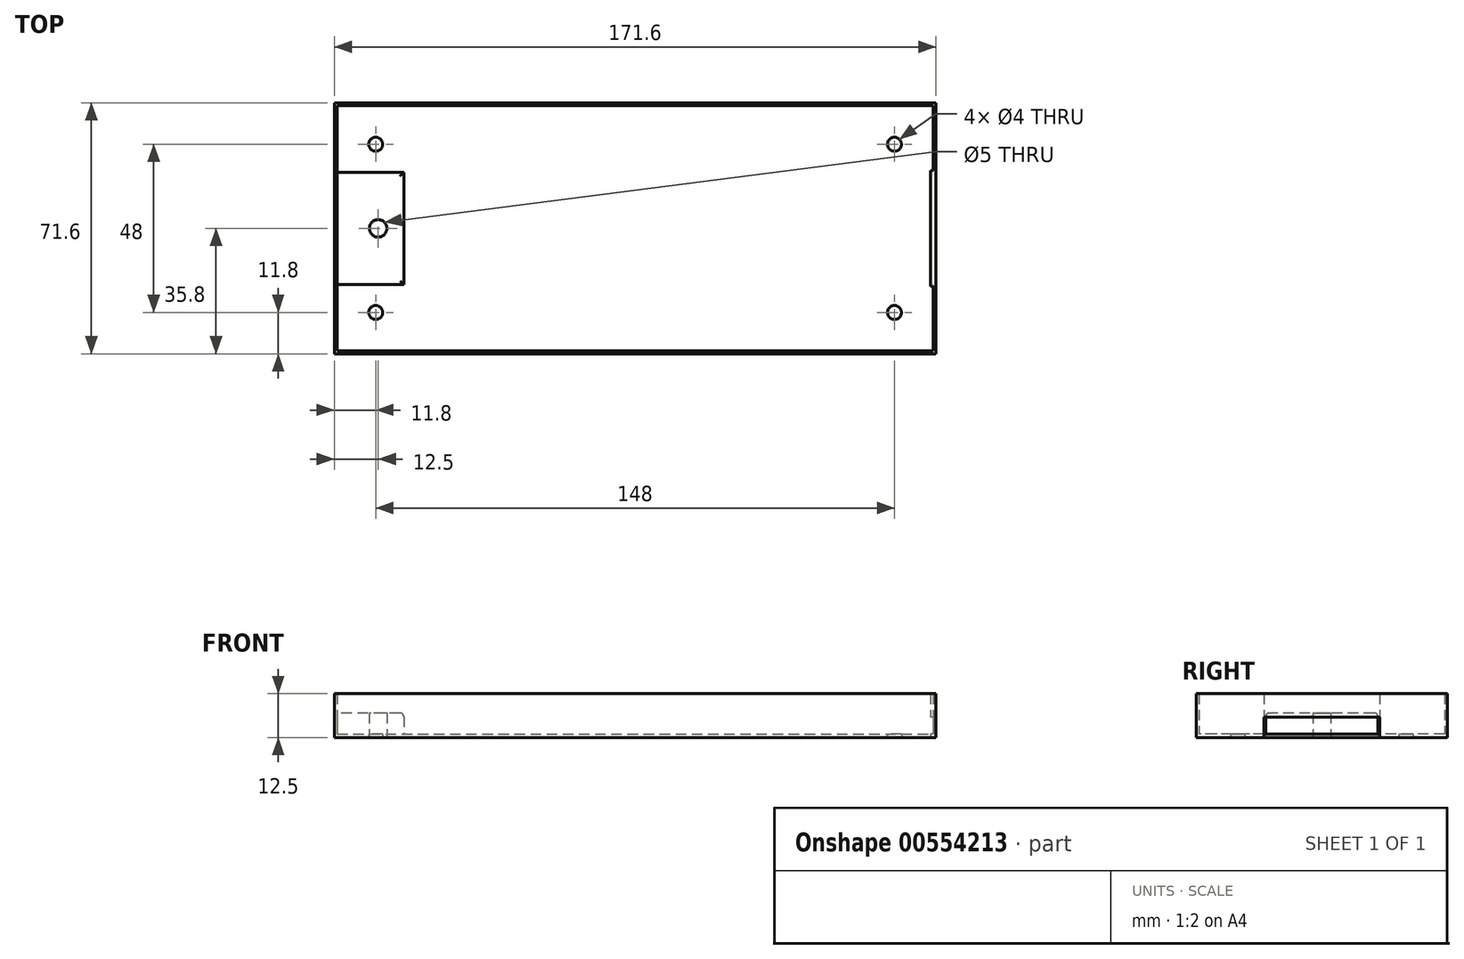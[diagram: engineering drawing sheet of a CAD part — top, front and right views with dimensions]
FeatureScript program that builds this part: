
annotation { "Feature Type Name" : "Feature", "Feature Type Description" : "" }
export const myFeature = defineFeature(function(context is Context, id is Id, definition is map)
    precondition{}
    {
        {
            var Q0;
            Q0=qCreatedBy(makeId("Top.planeOp"),FACE);
            var sketch = newSketch(context, id + "F0", { "sketchPlane" : qUnion([Q0])});
            skLineSegment(sketch, "E0.bottom", {"start": v(-85, 35) * mm, "end": v(85, 35) * mm});
            skLineSegment(sketch, "E0.top", {"start": v(-85, -35) * mm, "end": v(85, -35) * mm});
            skLineSegment(sketch, "E0.left", {"start": v(-85, 35) * mm, "end": v(-85, -35) * mm});
            skLineSegment(sketch, "E0.right", {"start": v(85, 35) * mm, "end": v(85, -35) * mm});
            skPoint(sketch, "E0.middle", {"position": v(0, 0) * mm});
            skCircle(sketch, "E1", {"center": v(74, -24) * mm, "radius": 2 * mm});
            skLineSegment(sketch, "E2", {"start": v(-150.17, 0) * mm, "end": v(130.9, 0) * mm, "construction": true});
            skCircle(sketch, "E3.MirrorC", {"center": v(74, 24) * mm, "radius": 2 * mm});
            skCircle(sketch, "E4", {"center": v(-74, -24) * mm, "radius": 2 * mm});
            skCircle(sketch, "E5.MirrorC", {"center": v(-74, 24) * mm, "radius": 2 * mm});
            skLineSegment(sketch, "E6.0", {"start": v(-85.8, 35.8) * mm, "end": v(85.8, 35.8) * mm});
            skLineSegment(sketch, "E6.1", {"start": v(-85.8, 35.8) * mm, "end": v(-85.8, -35.8) * mm});
            skLineSegment(sketch, "E6.2", {"start": v(-85.8, -35.8) * mm, "end": v(85.8, -35.8) * mm});
            skLineSegment(sketch, "E6.3", {"start": v(85.8, 35.8) * mm, "end": v(85.8, -35.8) * mm});
            skLineSegment(sketch, "E7.bottom", {"start": v(85.8, 16.5) * mm, "end": v(84.3, 16.5) * mm});
            skLineSegment(sketch, "E7.top", {"start": v(85.8, -16.5) * mm, "end": v(84.3, -16.5) * mm});
            skLineSegment(sketch, "E7.left", {"start": v(85.8, 16.5) * mm, "end": v(85.8, -16.5) * mm});
            skLineSegment(sketch, "E7.right", {"start": v(84.3, 16.5) * mm, "end": v(84.3, -16.5) * mm});
            skPoint(sketch, "E7.middle", {"position": v(85.05, 0) * mm});
            skLineSegment(sketch, "E8.bottom", {"start": v(-66, 16) * mm, "end": v(-85, 16) * mm});
            skLineSegment(sketch, "E8.top", {"start": v(-66, -16) * mm, "end": v(-85, -16) * mm});
            skLineSegment(sketch, "E8.left", {"start": v(-66, 16) * mm, "end": v(-66, -16) * mm});
            skLineSegment(sketch, "E8.right", {"start": v(-85, 16) * mm, "end": v(-85, -16) * mm});
            skPoint(sketch, "E8.middle", {"position": v(-85, 0) * mm});
            skCircle(sketch, "E9", {"center": v(-73.3, 0) * mm, "radius": 2.5 * mm});
            skPoint(sketch, "E9.centerSnap0", {"position": v(-75.5, 16) * mm});
            skSolve(sketch);
        }
        {
            var Q0;
            {var subQ3=sQuery(id+"F0.wireOp",EDGE,"E0.bottom");Q0=makeQuery(id+"F0.imprint","IMPRINT",FACE,{"disambiguationData":[TD([[makeQuery(id+"F0.imprint","IMPRINT",EDGE,{"derivedFrom":subQ3}),-1.0]])]});}
            var Q1;
            Q1=makeQuery(id+"F0.imprint","IMPRINT",FACE,{"disambiguationData":[TD([[makeQuery(id+"F0.imprint","IMPRINT",EDGE,{"derivedFrom":sQuery(id+"F0.wireOp",EDGE,"E8.bottom")}),1.0]])]});
            extrude(context, id + "F1", {"entities" : qUnion([Q0, Q1]), "depth" : 1 * mm, "offsetDistance" : 25 * mm});
        }
        {
            var Q0;
            Q0=makeQuery(id+"F0.imprint","IMPRINT",FACE,{"disambiguationData":[TD([[makeQuery(id+"F0.imprint","IMPRINT",EDGE,{"derivedFrom":sQuery(id+"F0.wireOp",EDGE,"E8.bottom")}),1.0]])]});
            extrude(context, id + "F2", {"entities" : qUnion([Q0]), "operationType" : NewBodyOperationType.ADD, "depth" : 7 * mm, "offsetDistance" : 25 * mm});
        }
        {
            var Q0;
            {var subQ5=sQuery(id+"F0.wireOp",EDGE,"E0.bottom");Q0=makeQuery(id+"F0.imprint","IMPRINT",FACE,{"disambiguationData":[TD([[makeQuery(id+"F0.imprint","IMPRINT",EDGE,{"derivedFrom":subQ5}),1.0]])]});}
            var Q1;
            Q1=makeQuery(id+"F0.imprint","IMPRINT",FACE,{"disambiguationData":[TD([[makeQuery(id+"F0.imprint","IMPRINT",EDGE,{"derivedFrom":sQuery(id+"F0.wireOp",EDGE,"E7.bottom")}),1.0]])]});
            extrude(context, id + "F3", {"entities" : qUnion([Q0, Q1]), "operationType" : NewBodyOperationType.ADD, "depth" : 12.5 * mm, "offsetDistance" : 25 * mm});
        }
        {
            var Q0;
            Q0=makeQuery(id+"F0.imprint","IMPRINT",FACE,{"disambiguationData":[TD([[makeQuery(id+"F0.imprint","IMPRINT",EDGE,{"derivedFrom":sQuery(id+"F0.wireOp",EDGE,"E7.bottom")}),1.0]])]});
            extrude(context, id + "F4", {"entities" : qUnion([Q0]), "operationType" : NewBodyOperationType.REMOVE, "depth" : 5.8 * mm, "offsetDistance" : 25 * mm});
        }
        {
            var Q0;
            Q0=makeQuery(id+"F2.opExtrude","CAP_EDGE",EDGE,{"disambiguationData":[OSD([sQuery(id+"F0.wireOp",EDGE,"E8.top")])],"isStart":false});
            var Q1;
            Q1=makeQuery(id+"F2.opExtrude","CAP_EDGE",EDGE,{"disambiguationData":[OSD([sQuery(id+"F0.wireOp",EDGE,"E8.bottom")])],"isStart":false});
            var Q2;
            Q2=makeQuery(id+"F2.opExtrude","CAP_EDGE",EDGE,{"disambiguationData":[OSD([sQuery(id+"F0.wireOp",EDGE,"E8.left")])],"isStart":false});
            fillet(context, id + "F5", {"entities" : qUnion([Q0, Q1, Q2]), "radius" : 1 * mm, "tangentPropagation" : true, "allowEdgeOverflow" : false});
        }
    });
